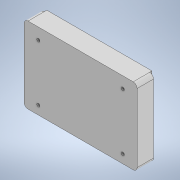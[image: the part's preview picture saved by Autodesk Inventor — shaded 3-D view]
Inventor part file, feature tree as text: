
AUTODESK INVENTOR PART (.ipt)
format: ipt  version: 2021 (Build 250183000, 183)  size: 156,672 bytes
history: native  units: mm
features: extrude x3, sketch x3, fillet x1
ambient origin geometry x8: Origin, YZ Plane, XZ Plane, XY Plane, X Axis, Y Axis, Z Axis, Center Point
bodies: Solid1 (feature_tree)
feature tree (7):
  extrude  "Extrusion1"  Depth=39.0mm
  extrude  "Extrusion2"  Depth=9.61mm
  extrude  "Extrusion3"  Depth=2.0mm
  fillet  "Fillet1"  Radius=5.8mm
  sketch  "Sketch1"  dims[d0=57.8mm d1=39.0mm]
  sketch  "Sketch2"  dims[d2=9.61mm d3=0.0mm d4=1.6mm]
  sketch  "Sketch3"  dims[d5=4.4mm d6=7.3mm d7=5.8mm d8=0.0mm d9=0.0mm d10=6.2mm d11=21.9mm d12=11.05mm d13=2.0mm d14=2.0mm d15=1.2mm d16=0.0mm d17=2.0mm]
